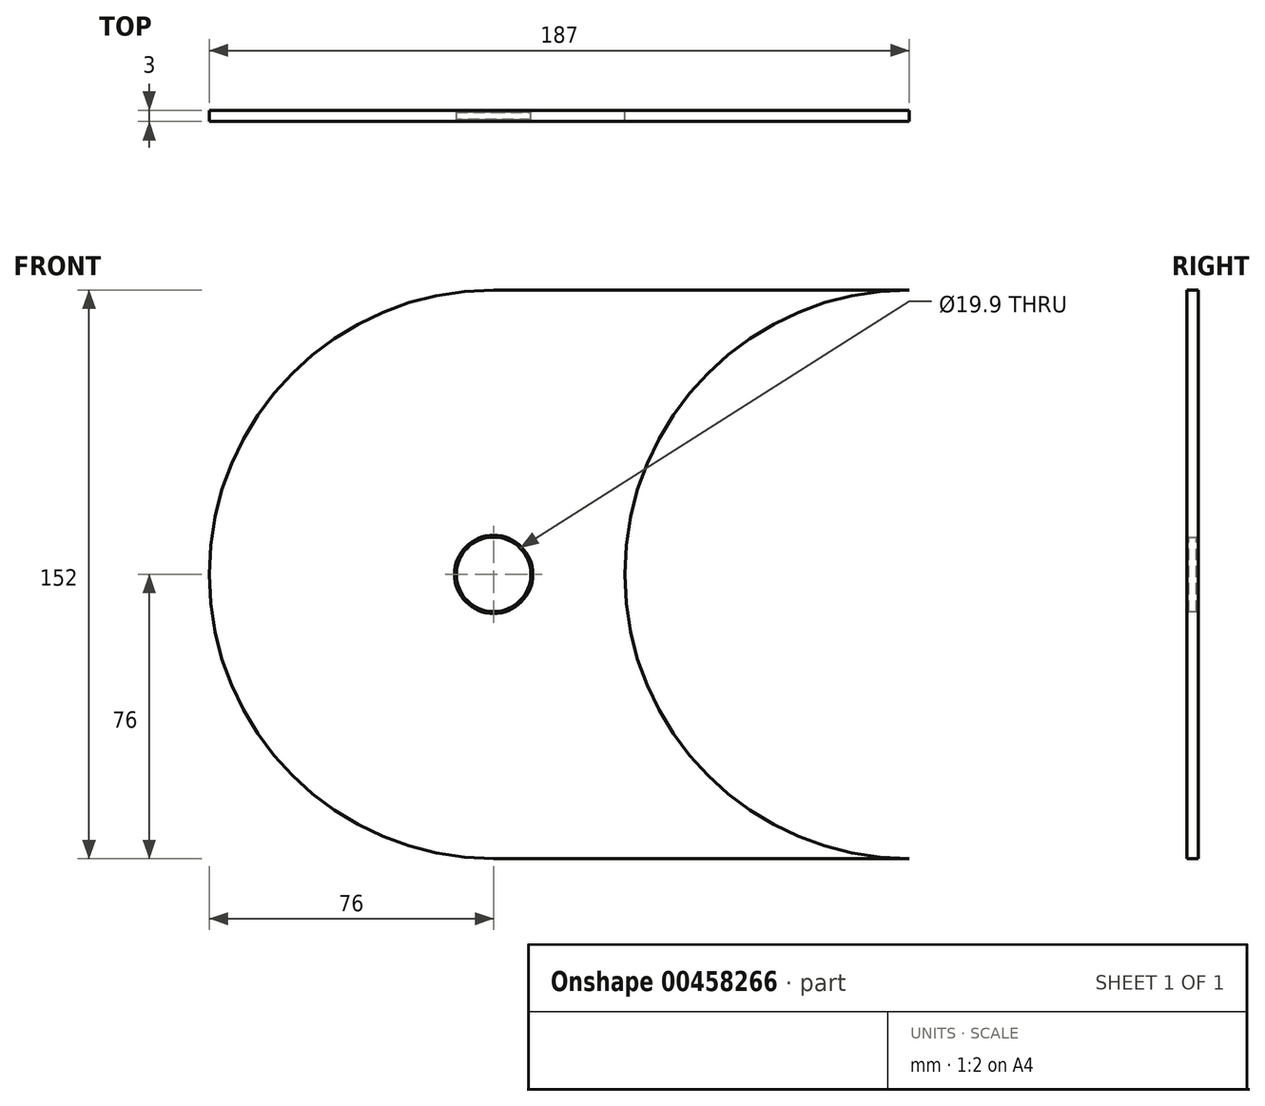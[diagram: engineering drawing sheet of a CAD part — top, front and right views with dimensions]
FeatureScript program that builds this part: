
annotation { "Feature Type Name" : "Feature", "Feature Type Description" : "" }
export const myFeature = defineFeature(function(context is Context, id is Id, definition is map)
    precondition{}
    {
        {
            var Q0;
            Q0=qCreatedBy(makeId("Front.planeOp"),FACE);
            var sketch = newSketch(context, id + "F0", { "sketchPlane" : qUnion([Q0])});
            skCircle(sketch, "E0", {"center": v(0, 0) * mm, "radius": 76 * mm});
            skCircle(sketch, "E1", {"center": v(111, 0) * mm, "radius": 76 * mm});
            skLineSegment(sketch, "E2", {"start": v(0, 76) * mm, "end": v(111, 76) * mm});
            skLineSegment(sketch, "E3", {"start": v(0, -76) * mm, "end": v(111, -76) * mm});
            skCircle(sketch, "E4", {"center": v(0, 0) * mm, "radius": 9.95 * mm});
            skCircle(sketch, "E5", {"center": v(111, 0) * mm, "radius": 12.45 * mm});
            skSolve(sketch);
        }
        {
            var Q0;
            {var subQ0=sQuery(id+"F0.wireOp",EDGE,"E3");Q0=makeQuery(id+"F0.imprint","IMPRINT",FACE,{"disambiguationData":[TD([[makeQuery(id+"F0.imprint","IMPRINT",EDGE,{"derivedFrom":subQ0}),1.0]])]});}
            var Q1;
            {var subQ0=sQuery(id+"F0.wireOp",EDGE,"E0");var subQ1=makeQuery(id+"F0.imprint","INTERSECT",VERTEX,{"derivedFrom":[subQ0,sQuery(id+"F0.wireOp",EDGE,"E2")]});Q1=makeQuery(id+"F0.imprint","IMPRINT",FACE,{"disambiguationData":[TD([[makeQuery(id+"F0.imprint","IMPRINT",EDGE,{"disambiguationData":[TD([[subQ1,1.0]])],"derivedFrom":subQ0}),1.0]])]});}
            var Q2;
            {var subQ0=sQuery(id+"F0.wireOp",EDGE,"E1");var subQ1=sQuery(id+"F0.wireOp",EDGE,"E0");var subQ2=makeQuery(id+"F0.imprint","INTERSECT",VERTEX,{"disambiguationData":[OD(0.0)],"derivedFrom":[subQ1,subQ0]});Q2=makeQuery(id+"F0.imprint","IMPRINT",FACE,{"disambiguationData":[TD([[makeQuery(id+"F0.imprint","IMPRINT",EDGE,{"disambiguationData":[TD([[subQ2,1.0]])],"derivedFrom":subQ1}),-1.0]])]});}
            var Q3;
            {var subQ0=sQuery(id+"F0.wireOp",EDGE,"E1");var subQ1=sQuery(id+"F0.wireOp",EDGE,"E0");var subQ2=makeQuery(id+"F0.imprint","INTERSECT",VERTEX,{"disambiguationData":[OD(0.0)],"derivedFrom":[subQ1,subQ0]});Q3=makeQuery(id+"F0.imprint","IMPRINT",FACE,{"disambiguationData":[TD([[makeQuery(id+"F0.imprint","IMPRINT",EDGE,{"disambiguationData":[TD([[subQ2,1.0]])],"derivedFrom":subQ1}),1.0]])]});}
            var Q4;
            {var subQ0=sQuery(id+"F0.wireOp",EDGE,"E2");Q4=makeQuery(id+"F0.imprint","IMPRINT",FACE,{"disambiguationData":[TD([[makeQuery(id+"F0.imprint","IMPRINT",EDGE,{"derivedFrom":subQ0}),-1.0]])]});}
            extrude(context, id + "F1", {"entities" : qUnion([Q0, Q1, Q2, Q3, Q4]), "depth" : 3 * mm, "offsetDistance" : 25 * mm});
        }
        {
            var Q0;
            Q0=makeQuery(id+"F1.opExtrude","CAP_EDGE",EDGE,{"disambiguationData":[OSD([sQuery(id+"F0.wireOp",EDGE,"E4")])],"isStart":false});
            var Q1;
            Q1=makeQuery(id+"F1.opExtrude","CAP_EDGE",EDGE,{"disambiguationData":[OSD([sQuery(id+"F0.wireOp",EDGE,"E4")])],"isStart":true});
            var Q2;
            Q2=makeQuery(id+"F1.opExtrude","CAP_EDGE",EDGE,{"disambiguationData":[OSD([sQuery(id+"F0.wireOp",EDGE,"E5")])],"isStart":true});
            var Q3;
            Q3=makeQuery(id+"F1.opExtrude","CAP_EDGE",EDGE,{"disambiguationData":[OSD([sQuery(id+"F0.wireOp",EDGE,"E5")])],"isStart":false});
            chamfer(context, id + "F2", {"entities" : qUnion([Q0, Q1, Q2, Q3]), "width" : 0.5 * mm, "tangentPropagation" : true});
        }
    });
